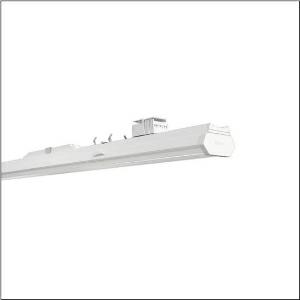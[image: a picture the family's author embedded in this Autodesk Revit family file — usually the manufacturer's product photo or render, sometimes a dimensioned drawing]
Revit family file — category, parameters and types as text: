
# Revit family: licross_r__11_protected_mo_51td127n485g_dbd9
name_source: partatom
category: Lighting Fixtures
units: mm (PartAtom-declared; Revit-internal decimal feet)

## family parameters
Cut with Voids When Loaded = No
Host = Face
Light Source = No
Part Type = Normal
Room Calculation Point = No
Round Connector Dimension = Use Diameter
Shared = No

## types (1)
- Licross® 11 Protected MO (1 x LED, 8720 lm, 48.6 W, 4000K)
    Apparent Load = 49 VA
    CIE Flux Codes = 73 92 98 99 100
    Color Rendering = 80
    Color Temperature = 4000K
    Default Elevation = 1800 mm
    Description = Licross® 11 Protected MO, luminaire insert, of sheet steel, galvanised, coil coated, white, length: 1.500mm, width: 90mm, height: 101mm, LED rated luminous flux: 8.720lm, light colour: 840, control gear: ON/OFF, control gear: ECG, with plug, 3-pole, with phase selection, mains connection: 220..240V, AC, 50/60Hz, halogen-free wiring, primary light control with lens, of plastic, primary optical cover: cover, of PMMA, light emission: direct with ceiling illumination distribution, primary light characteristic: symmetric, protection rating (complete): IP54, insulation class (complete): insulation class I (protective earthing), certification: CE, ENEC, VDE, UKCA, protection symbol: D if used in an environment with non-conductive dust loads with corresponding accessories, impact resistance: IK06, corresponds to IFS (International Featured Standards) requirements for safety and quality in the food industry, reducing of maximum allowable ambient temperature of 5°C with ceiling mounting, LABS conformity tested according to VDMA 24364:2018-05, packaging unit: 1 piece
    Height = 92 mm
    Lamp = 1 x LED
    Lamp Light Flux = 8720 lm
    Lamp Power = 48.6 W
    Lamp count = 1
    Length = 1500 mm
    Luminous efficacy = 179 lm/W
    Manufacturer = Siteco
    ModVariant = No
    Model = 51TD127N485G
    Mounting Place = Ceiling
    Mounting Type = Pendant
    Number of Poles = 1
    OnlyDefault = Yes
    Power Factor = 1
    Product Name = Licross® 11 Protected MO
    Product group = luminaire insert
    ProductGroupID = 902
    Protection Class = Protection class I
    Protection Degree = IP 54
    RLX_Detail_Level = 1
    RlxData = <blob elided: 20641 chars, md5=8c00f5e8>
    Socket = socket
    Standby Power = 0 W
    System Light Flux = 8720 lm
    System Power = 49 W
    Type Comments = Product without accessories
    Type Image = l_1256145.jpg
    URL = http://relux.com
    VarID = ---
    Voltage = 0 V
    Weight = 0.00 kg
    Width = 88 mm

## geometry (parser evidence)
native form markers: Blend x4, Sweep x10
no freeform markers — native parametric forms only
